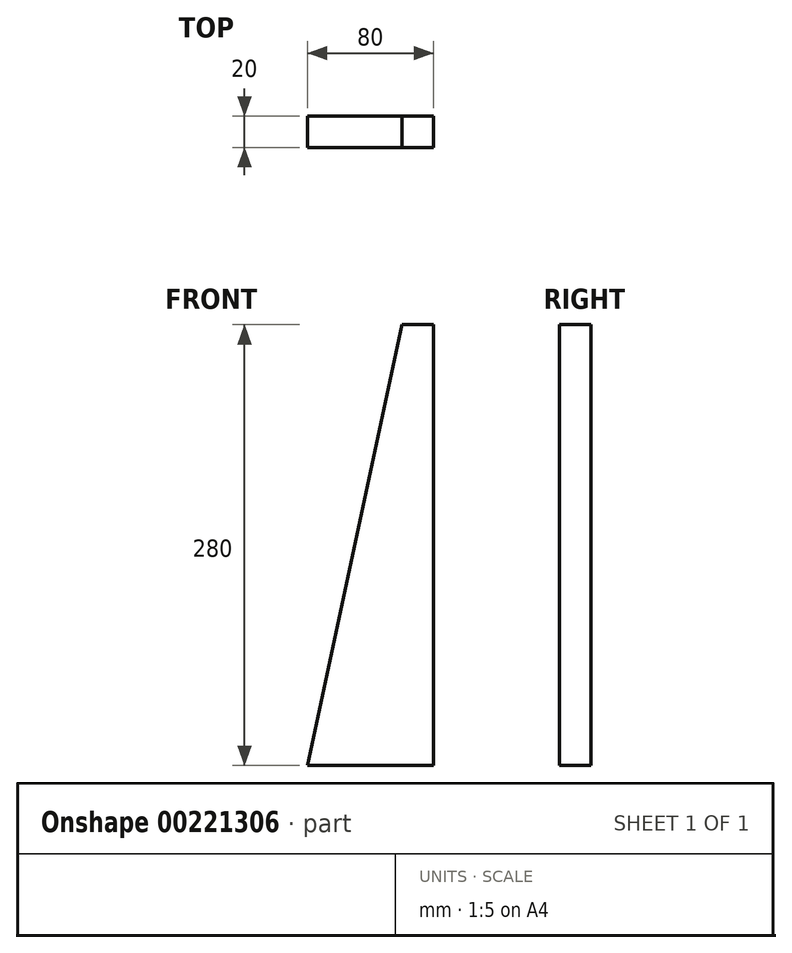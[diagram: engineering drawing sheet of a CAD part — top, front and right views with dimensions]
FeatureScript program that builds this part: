
annotation { "Feature Type Name" : "Feature", "Feature Type Description" : "" }
export const myFeature = defineFeature(function(context is Context, id is Id, definition is map)
    precondition{}
    {
        {
            var Q0;
            Q0=qCreatedBy(makeId("Front.planeOp"),FACE);
            var sketch = newSketch(context, id + "F0", { "sketchPlane" : qUnion([Q0])});
            skLineSegment(sketch, "E0", {"start": v(-36.86, 140.43) * mm, "end": v(-16.86, 140.43) * mm});
            skLineSegment(sketch, "E1", {"start": v(-16.86, 140.43) * mm, "end": v(-16.86, -139.57) * mm});
            skLineSegment(sketch, "E2", {"start": v(-16.86, -139.57) * mm, "end": v(-96.86, -139.57) * mm});
            skLineSegment(sketch, "E3", {"start": v(-96.86, -139.57) * mm, "end": v(-36.86, 140.43) * mm});
            skSolve(sketch);
        }
        {
            var Q0;
            Q0=makeQuery(id+"F0.imprint","IMPRINT",FACE,{"disambiguationData":[TD([[makeQuery(id+"F0.imprint","IMPRINT",EDGE,{"derivedFrom":sQuery(id+"F0.wireOp",EDGE,"E0")}),-1.0]])]});
            extrude(context, id + "F1", {"entities" : qUnion([Q0]), "depth" : 20 * mm});
        }
    });
